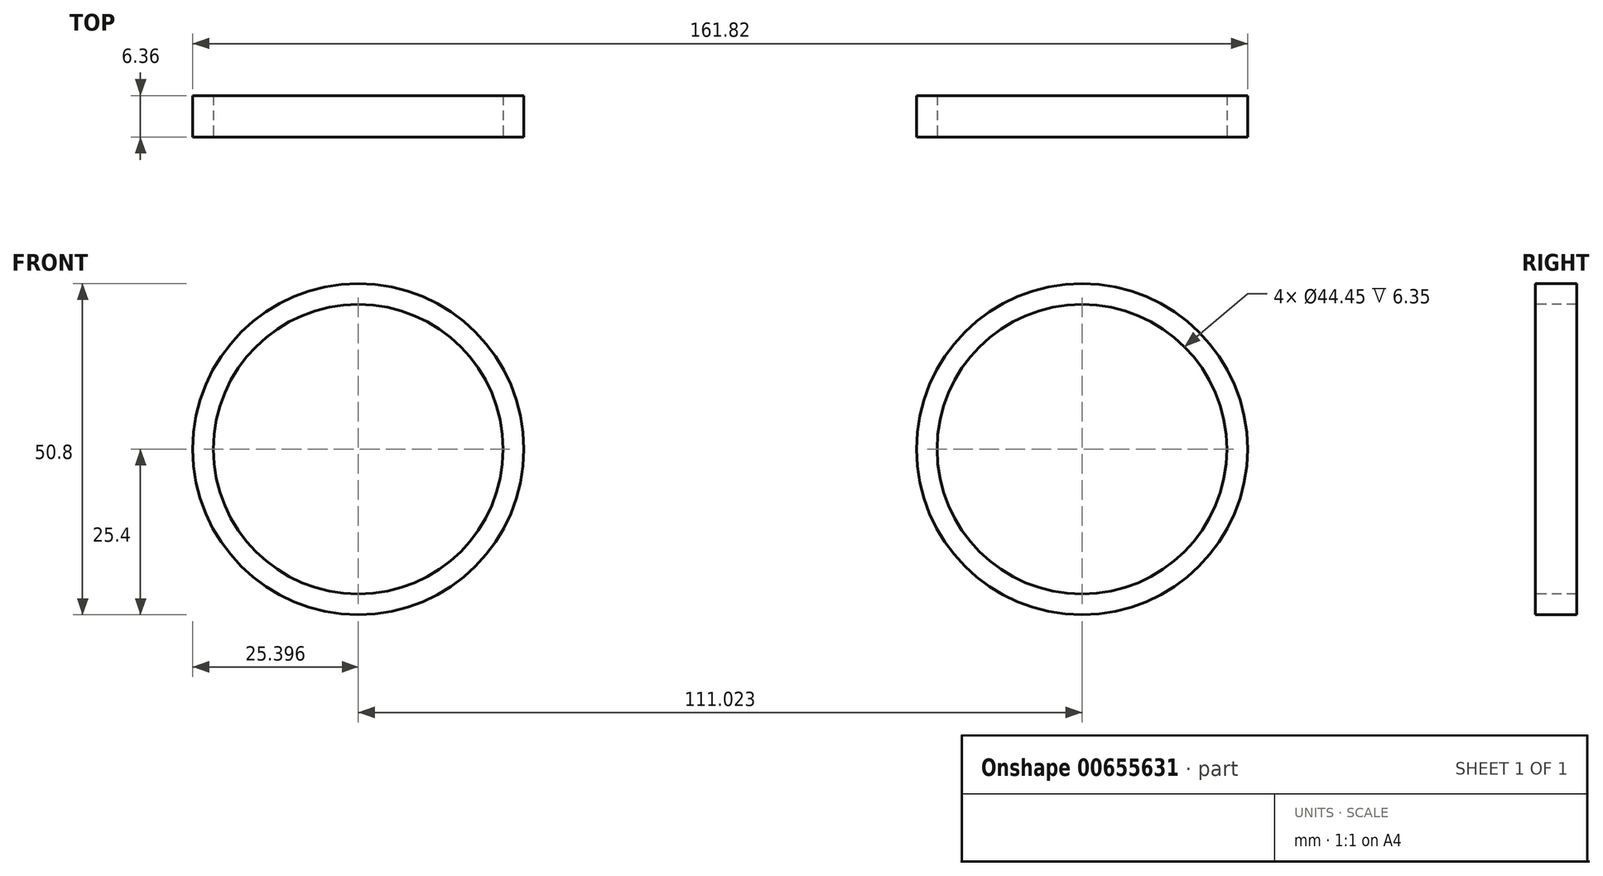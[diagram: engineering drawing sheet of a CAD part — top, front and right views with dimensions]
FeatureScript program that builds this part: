
annotation { "Feature Type Name" : "Feature", "Feature Type Description" : "" }
export const myFeature = defineFeature(function(context is Context, id is Id, definition is map)
    precondition{}
    {
        {
            var Q0;
            Q0=qCreatedBy(makeId("Front.planeOp"),FACE);
            var sketch = newSketch(context, id + "F0", { "sketchPlane" : qUnion([Q0])});
            skCircle(sketch, "E0", {"center": v(59.68, 0) * mm, "radius": 25.4 * mm});
            skCircle(sketch, "E1", {"center": v(-51.34, 0) * mm, "radius": 25.4 * mm});
            skCircle(sketch, "E2", {"center": v(-51.34, 0) * mm, "radius": 22.23 * mm});
            skCircle(sketch, "E3", {"center": v(59.68, 0) * mm, "radius": 22.23 * mm});
            skSolve(sketch);
        }
        {
            var Q0;
            Q0 = qSketchRegion(id + "F0", true);
            extrude(context, id + "F1", {"entities" : qUnion([Q0]), "endBound" : BoundingType.SYMMETRIC, "depth" : 6.35 * mm, "offsetDistance" : 25.4 * mm});
        }
        {
            var Q0;
            Q0 = qSketchRegion(id + "F0", true);
            extrude(context, id + "F2", {"entities" : qUnion([Q0]), "endBound" : BoundingType.SYMMETRIC, "oppositeDirection" : true, "depth" : 6.35 * mm, "offsetDistance" : 25.4 * mm});
        }
    });
